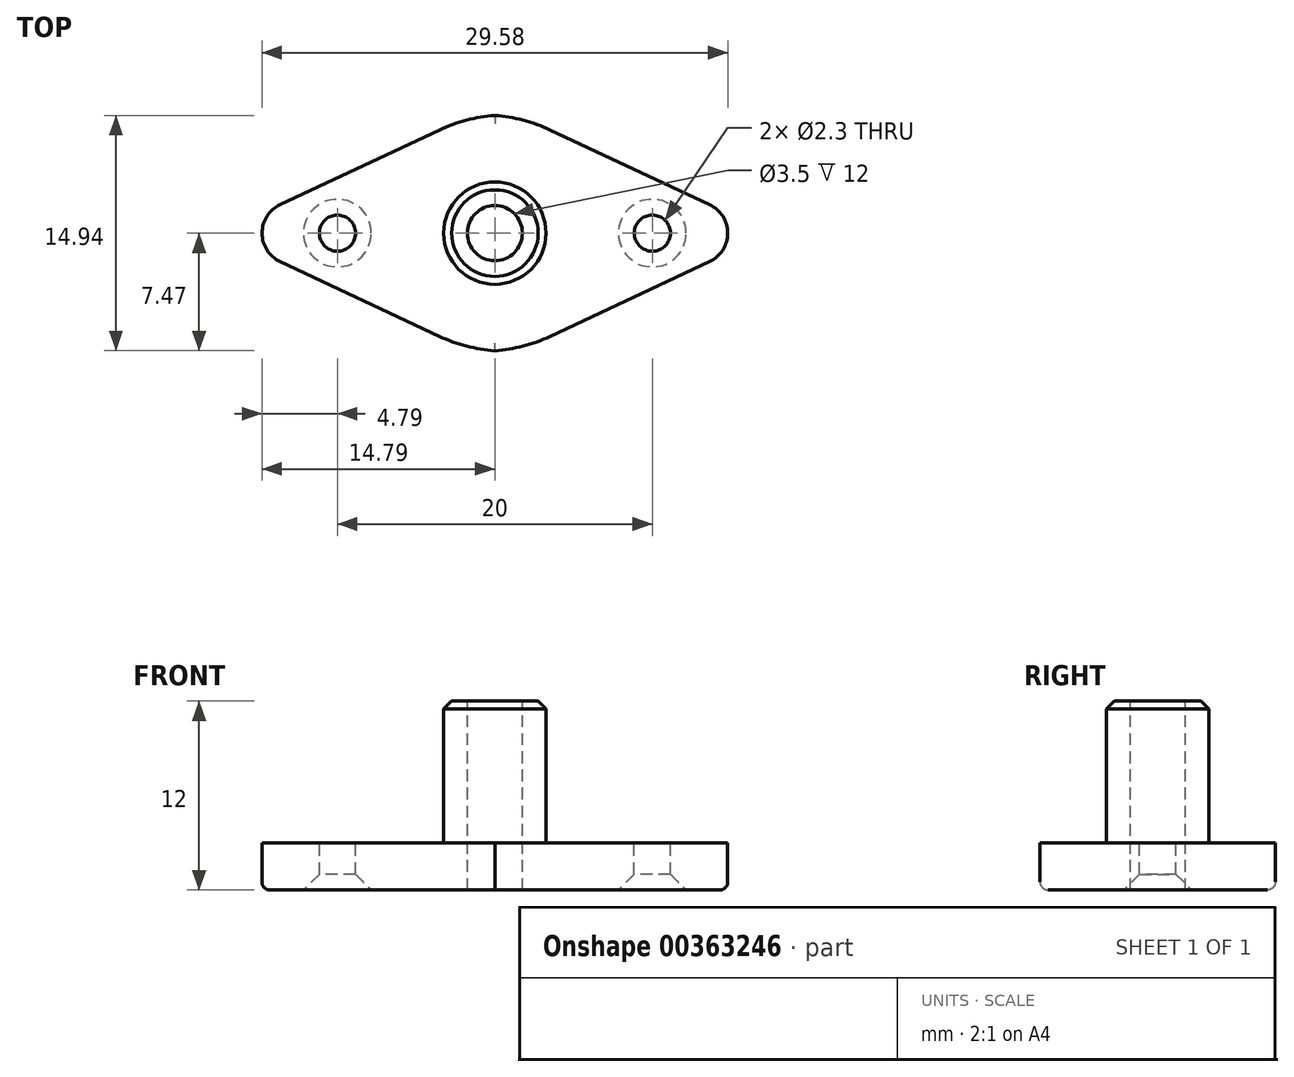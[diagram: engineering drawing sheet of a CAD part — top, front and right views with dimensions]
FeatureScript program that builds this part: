
annotation { "Feature Type Name" : "Feature", "Feature Type Description" : "" }
export const myFeature = defineFeature(function(context is Context, id is Id, definition is map)
    precondition{}
    {
        {
            var Q0;
            Q0=qCreatedBy(makeId("Top.planeOp"),FACE);
            var sketch = newSketch(context, id + "F0", { "sketchPlane" : qUnion([Q0])});
            skCircle(sketch, "E0", {"center": v(0, 0) * mm, "radius": 7.5 * mm, "construction": true});
            skLineSegment(sketch, "E1.bottom", {"start": v(17.5, -7.5) * mm, "end": v(-17.5, -7.5) * mm, "construction": true});
            skLineSegment(sketch, "E1.top", {"start": v(17.5, 7.5) * mm, "end": v(-17.5, 7.5) * mm, "construction": true});
            skLineSegment(sketch, "E1.left", {"start": v(17.5, -7.5) * mm, "end": v(17.5, 7.5) * mm, "construction": true});
            skLineSegment(sketch, "E1.right", {"start": v(-17.5, -7.5) * mm, "end": v(-17.5, 7.5) * mm, "construction": true});
            skLineSegment(sketch, "E2", {"start": v(-17.5, 0) * mm, "end": v(-1.5, 7.5) * mm});
            skLineSegment(sketch, "E3", {"start": v(1.5, 7.5) * mm, "end": v(17.5, 0) * mm});
            skLineSegment(sketch, "E4", {"start": v(17.5, 0) * mm, "end": v(1.5, -7.5) * mm});
            skLineSegment(sketch, "E5", {"start": v(-1.5, -7.5) * mm, "end": v(-17.5, 0) * mm});
            skLineSegment(sketch, "E6", {"start": v(-1.5, 7.5) * mm, "end": v(1.5, 7.5) * mm});
            skLineSegment(sketch, "E7", {"start": v(-1.5, 7.5) * mm, "end": v(-1.5, -7.5) * mm, "construction": true});
            skLineSegment(sketch, "E8", {"start": v(1.5, 7.5) * mm, "end": v(1.5, -7.5) * mm, "construction": true});
            skLineSegment(sketch, "E9", {"start": v(-1.5, -7.5) * mm, "end": v(1.5, -7.5) * mm});
            skSolve(sketch);
        }
        {
            var Q0;
            Q0=makeQuery(id+"F0.imprint","IMPRINT",FACE,{"disambiguationData":[TD([[makeQuery(id+"F0.imprint","IMPRINT",EDGE,{"derivedFrom":sQuery(id+"F0.wireOp",EDGE,"E2")}),-1.0]])]});
            extrude(context, id + "F1", {"entities" : qUnion([Q0]), "depth" : 3 * mm});
        }
        {
            var Q0;
            Q0=makeQuery(id+"F1.opExtrude","SWEPT_EDGE",EDGE,{"disambiguationData":[OSD([sQuery(id+"F0.wireOp",EDGE,"E2"),sQuery(id+"F0.wireOp",EDGE,"E5")])]});
            var Q1;
            Q1=makeQuery(id+"F1.opExtrude","SWEPT_EDGE",EDGE,{"disambiguationData":[OSD([sQuery(id+"F0.wireOp",EDGE,"E3"),sQuery(id+"F0.wireOp",EDGE,"E4")])]});
            fillet(context, id + "F2", {"entities" : qUnion([Q0, Q1]), "radius" : 2 * mm, "tangentPropagation" : true, "allowEdgeOverflow" : false});
        }
        {
            var Q0;
            Q0=makeQuery(id+"F1.opExtrude","SWEPT_EDGE",EDGE,{"disambiguationData":[OSD([sQuery(id+"F0.wireOp",EDGE,"E4"),sQuery(id+"F0.wireOp",EDGE,"E5")])]});
            var Q1;
            Q1=makeQuery(id+"F1.opExtrude","SWEPT_EDGE",EDGE,{"disambiguationData":[OSD([sQuery(id+"F0.wireOp",EDGE,"E2"),sQuery(id+"F0.wireOp",EDGE,"E3")])]});
            fillet(context, id + "F3", {"entities" : qUnion([Q0, Q1]), "radius" : 10 * mm, "tangentPropagation" : true, "allowEdgeOverflow" : false});
        }
        {
            var Q0;
            Q0=makeQuery(id+"F1.opExtrude","CAP_FACE",FACE,{"disambiguationData":[OSD([sQuery(id+"F0.wireOp",EDGE,"E2"),sQuery(id+"F0.wireOp",EDGE,"E3"),sQuery(id+"F0.wireOp",EDGE,"E4"),sQuery(id+"F0.wireOp",EDGE,"E5"),sQuery(id+"F0.wireOp",EDGE,"E6"),sQuery(id+"F0.wireOp",EDGE,"E9")])],"isStart":false});
            var sketch = newSketch(context, id + "F4", { "sketchPlane" : qUnion([Q0])});
            skCircle(sketch, "E10", {"center": v(0, 0) * mm, "radius": 3.25 * mm});
            skLineSegment(sketch, "E11", {"start": v(-14.79, 0) * mm, "end": v(14.79, 0) * mm, "construction": true});
            skCircle(sketch, "E12", {"center": v(-10, 0) * mm, "radius": 1.15 * mm});
            skCircle(sketch, "E13", {"center": v(10, 0) * mm, "radius": 1.15 * mm});
            skSolve(sketch);
        }
        {
            var Q0;
            Q0=makeQuery(id+"F4.imprint","IMPRINT",FACE,{"disambiguationData":[TD([[makeQuery(id+"F4.imprint","IMPRINT",EDGE,{"derivedFrom":sQuery(id+"F4.wireOp",EDGE,"E10")}),1.0]])]});
            extrude(context, id + "F5", {"entities" : qUnion([Q0]), "operationType" : NewBodyOperationType.ADD, "depth" : 9 * mm});
        }
        {
            var Q0;
            Q0=makeQuery(id+"F5.opExtrude","CAP_FACE",FACE,{"disambiguationData":[OSD([sQuery(id+"F4.wireOp",EDGE,"E10")])],"isStart":false});
            var sketch = newSketch(context, id + "F6", { "sketchPlane" : qUnion([Q0])});
            skCircle(sketch, "E14", {"center": v(0, 0) * mm, "radius": 1.75 * mm});
            skSolve(sketch);
        }
        {
            var Q0;
            Q0=makeQuery(id+"F6.imprint","IMPRINT",FACE,{"disambiguationData":[TD([[makeQuery(id+"F6.imprint","IMPRINT",EDGE,{"derivedFrom":sQuery(id+"F6.wireOp",EDGE,"E14")}),1.0]])]});
            extrude(context, id + "F7", {"entities" : qUnion([Q0]), "operationType" : NewBodyOperationType.REMOVE, "endBound" : BoundingType.THROUGH_ALL, "oppositeDirection" : true, "depth" : 25 * mm});
        }
        {
            var Q0;
            Q0=makeQuery(id+"F5.opExtrude","CAP_EDGE",EDGE,{"disambiguationData":[OSD([sQuery(id+"F4.wireOp",EDGE,"E10")])],"isStart":false});
            chamfer(context, id + "F8", {"entities" : qUnion([Q0]), "width" : .5 * mm, "tangentPropagation" : true});
        }
        {
            var Q0;
            Q0=makeQuery(id+"F4.imprint","IMPRINT",FACE,{"disambiguationData":[TD([[makeQuery(id+"F4.imprint","IMPRINT",EDGE,{"derivedFrom":sQuery(id+"F4.wireOp",EDGE,"E12")}),1.0]])]});
            var Q1;
            Q1=makeQuery(id+"F4.imprint","IMPRINT",FACE,{"disambiguationData":[TD([[makeQuery(id+"F4.imprint","IMPRINT",EDGE,{"derivedFrom":sQuery(id+"F4.wireOp",EDGE,"E13")}),1.0]])]});
            extrude(context, id + "F9", {"entities" : qUnion([Q0, Q1]), "operationType" : NewBodyOperationType.REMOVE, "endBound" : BoundingType.THROUGH_ALL, "oppositeDirection" : true, "depth" : 25 * mm});
        }
        {
            var Q0;
            Q0=makeQuery(id+"F9.boolean.opBoolean","INTERSECT",EDGE,{"derivedFrom":[makeQuery(id+"F1.opExtrude","CAP_FACE",FACE,{"disambiguationData":[OSD([sQuery(id+"F0.wireOp",EDGE,"E2"),sQuery(id+"F0.wireOp",EDGE,"E3"),sQuery(id+"F0.wireOp",EDGE,"E4"),sQuery(id+"F0.wireOp",EDGE,"E5"),sQuery(id+"F0.wireOp",EDGE,"E6"),sQuery(id+"F0.wireOp",EDGE,"E9")])],"isStart":true}),makeQuery(id+"F9.opExtrude","SWEPT_FACE",FACE,{"disambiguationData":[OSD([sQuery(id+"F4.wireOp",EDGE,"E12")])]})]});
            var Q1;
            Q1=makeQuery(id+"F9.boolean.opBoolean","INTERSECT",EDGE,{"derivedFrom":[makeQuery(id+"F1.opExtrude","CAP_FACE",FACE,{"disambiguationData":[OSD([sQuery(id+"F0.wireOp",EDGE,"E2"),sQuery(id+"F0.wireOp",EDGE,"E3"),sQuery(id+"F0.wireOp",EDGE,"E4"),sQuery(id+"F0.wireOp",EDGE,"E5"),sQuery(id+"F0.wireOp",EDGE,"E6"),sQuery(id+"F0.wireOp",EDGE,"E9")])],"isStart":true}),makeQuery(id+"F9.opExtrude","SWEPT_FACE",FACE,{"disambiguationData":[OSD([sQuery(id+"F4.wireOp",EDGE,"E13")])]})]});
            chamfer(context, id + "F10", {"entities" : qUnion([Q0, Q1]), "width" : 1 * mm, "tangentPropagation" : true});
        }
        {
            var Q0;
            Q0=makeQuery(id+"F1.opExtrude","CAP_EDGE",EDGE,{"disambiguationData":[OSD([sQuery(id+"F0.wireOp",EDGE,"E5")])],"isStart":true});
            var Q1;
            Q1=makeQuery(id+"F1.opExtrude","CAP_EDGE",EDGE,{"disambiguationData":[OSD([sQuery(id+"F0.wireOp",EDGE,"E4")])],"isStart":true});
            fillet(context, id + "F11", {"entities" : qUnion([Q0, Q1]), "radius" : .5 * mm, "tangentPropagation" : true, "allowEdgeOverflow" : false});
        }
    });
